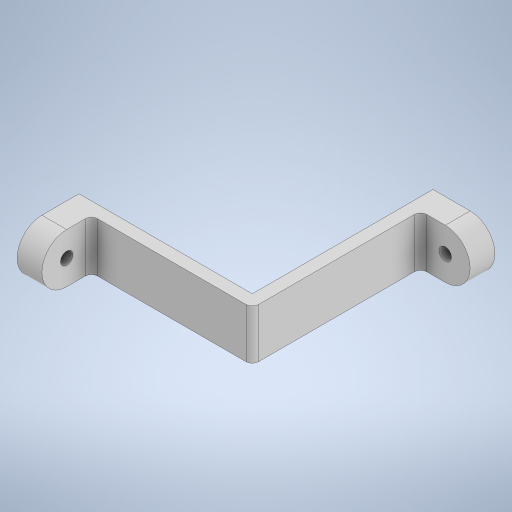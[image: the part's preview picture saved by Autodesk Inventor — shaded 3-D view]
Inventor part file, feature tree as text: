
AUTODESK INVENTOR PART (.ipt)
format: ipt  version: 2024 (Build 280153000, 153)  size: 311,296 bytes
history: native  units: in
note: dims shown in document units (in); Inventor stores cm internally (conversion verified against a paired STEP export)
features: extrude x5, sketch x5, fillet x4, projected_geometry x2
ambient origin geometry x8: Origin, YZ Plane, XZ Plane, XY Plane, X Axis, Y Axis, Z Axis, Center Point
bodies: Solid1 (feature_tree)
feature tree (16):
  extrude  "Extrusion1"  Depth=0.5in
  fillet  "Fillet1"  Radius=0.25in
  fillet  "Fillet2"  Radius=0.5in
  extrude  "Extrusion2"  Depth=0.5in
  extrude  "Extrusion3"  Depth=1.0in TaperAngle=0.0deg
  extrude  "Extrusion4"  Depth=0.5in
  fillet  "Fillet3"  Radius=0.25in
  fillet  "Fillet4"  Radius=0.25in
  extrude  "Extrusion5"  Depth=0.5in
  sketch  "Sketch1"  dims[d0=3.4in d1=7.1in d2=0.25in d3=0.5in]
  sketch  "Sketch2"  dims[d4=1.0in d5=0.5in]
  projected_geometry  "Projected Loop1"
  projected_geometry  "Projected Loop2"
  sketch  "Sketch3"  dims[d6=1.0in d7=1.0in d8=0.0in]
  sketch  "Sketch4"  dims[d9=0.125in d10=0.5in d11=0.25in d12=0.25in]
  sketch  "Sketch5"  dims[d13=1.0in d14=0.0in d15=0.5in d16=1.0in d17=0.0in d18=0.0in d19=0.0in d20=0.5in d21=0.125in d22=0.25in d23=1.0in d24=0.0in]
